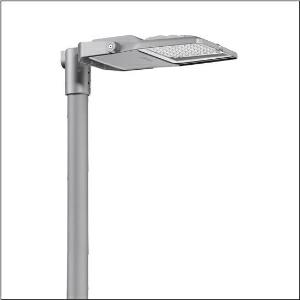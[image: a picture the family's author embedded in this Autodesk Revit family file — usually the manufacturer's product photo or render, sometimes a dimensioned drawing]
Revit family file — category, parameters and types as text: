
# Revit family: floodlight_fl_21_iq_mini___pl64_5xa7771b2e3a_ab64
name_source: partatom
category: Lighting Fixtures
units: mm (PartAtom-declared; Revit-internal decimal feet)

## family parameters
Cut with Voids When Loaded = No
Host = Face
Light Source = No
Part Type = Normal
Room Calculation Point = No
Round Connector Dimension = Use Diameter
Shared = No

## types (1)
- --- (1 x LED, 6020 lm, 45.5 W, 3000K)
    Apparent Load = 46 VA
    CIE Flux Codes = 28 80 98 100 100
    Color Rendering = 70
    Color Temperature = 3000K
    Default Elevation = 1800 mm
    Description = Floodlight FL 21 iQ mini, floodlight, primary light control with lens, of PMMA, primary optical cover: protective disc, of toughened safety glass, transparent, light distribution: PL64, light emission: direct distribution, installation type: surface-mounted, LED, High Power LED, rated luminous flux: 6.020lm, luminous efficacy: 132lm/W, light colour: 730, colour temperature: 3000K, control: Auto-Match, Temp-Guard, Lumen-Switch, Night-Set, Smart-Wire, Light-Fading, Desk-Remote (wireless, voltage-free reading and setting of iQ features in the workshop via application-optimized NFC function/RFID function), optimised constant luminous flux control (CLO 2.0), with terminal, 6-pole, mains connection: 220..240V, AC, 50/60Hz, start of lifetime: 46W, end of service life: 48W, reduction: 22W, luminaire housing, of diecast aluminium, powder-coated, Siteco® metallic grey (DB 702S), corrosivity category C5 mid according to DIN EN ISO 12944, sealing non-destructively replaceable, please order mast flange separately, mast bracket, of steel, galvanised, powder-coated, Siteco® metallic grey (DB 702S), protection rating (complete): IP66, insulation class (complete): insulation class II (safety insulation), certification: CE, ENEC, VDE, protection symbol: D, impact resistance: IK08, permissible operating ambient temperature: -40..+40°C, permissible operating ambient temperature for outdoor applications: -40..+50°C, standard: DIN EN 12944, LABS conformity tested according to VDMA 24364:2018-05, packaging unit: 1 piece

Light Distribution: PL64
    Height = 70 mm
    Lamp = 1 x LED
    Lamp Light Flux = 6020 lm
    Lamp Power = 45.5 W
    Lamp count = 1
    Length = 485 mm
    Luminous efficacy = 132 lm/W
    Manufacturer = Siteco
    ModVariant = No
    Model = 5XA7771B2E3A
    Number of Poles = 1
    OnlyDefault = Yes
    Power Factor = 1
    Product Name = Floodlight FL 21 iQ mini | PL64
    Product group = floodlight | pylon annexe
    ProductGroupID = 6200
    Protection Class = Protection class II
    Protection Degree = IP 66
    RLX_Detail_Level = 1
    RLX_Emergency_Light_Flux = 0 lm
    RLX_Emergency_Type = 0
    RLX_Emergency_Type_DB = No
    RlxData = <blob elided: 101177 chars, md5=b52aecc6>
    Socket = socket
    Standby Power = 0 W
    System Light Flux = 6020 lm
    System Power = 46 W
    Type Comments = factory setting: luminous flux: 100 % | dim-lin: 254 | 463 mA
    Type Image = l_1007125.jpg
    URL = http://relux.com
    VarID = @adj_099453
    Voltage = 0 V
    Weight = 0.00 kg
    Width = 337 mm

## geometry (parser evidence)
native form markers: Blend x4, Sweep x12
no freeform markers — native parametric forms only
